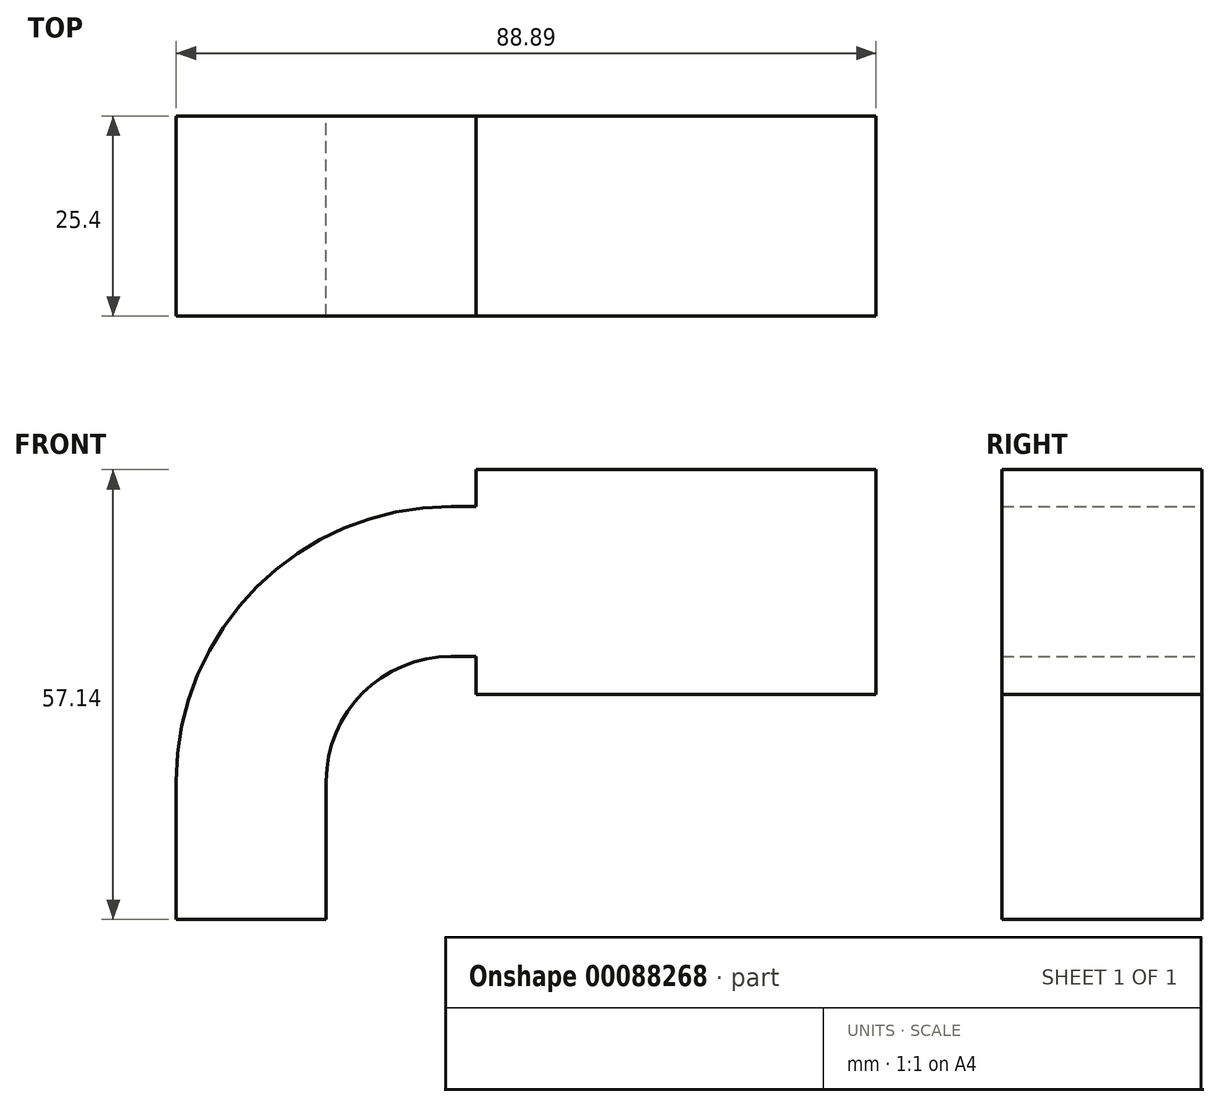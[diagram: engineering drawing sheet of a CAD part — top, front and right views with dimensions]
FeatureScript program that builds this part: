
annotation { "Feature Type Name" : "Feature", "Feature Type Description" : "" }
export const myFeature = defineFeature(function(context is Context, id is Id, definition is map)
    precondition{}
    {
        {
            var Q0;
            Q0=qCreatedBy(makeId("Front.planeOp"),FACE);
            var sketch = newSketch(context, id + "F0", { "sketchPlane" : qUnion([Q0])});
            skLineSegment(sketch, "E0.bottom", {"start": v(41.27, 9.53) * mm, "end": v(-41.28, 9.53) * mm});
            skLineSegment(sketch, "E0.top", {"start": v(41.28, -9.52) * mm, "end": v(-41.28, -9.53) * mm});
            skLineSegment(sketch, "E0.left", {"start": v(41.28, 9.53) * mm, "end": v(41.28, -9.52) * mm});
            skLineSegment(sketch, "E0.right", {"start": v(-41.28, 9.53) * mm, "end": v(-41.28, -9.53) * mm});
            skPoint(sketch, "E0.middle", {"position": v(0, 0) * mm});
            skLineSegment(sketch, "E1.bottom", {"start": v(111.12, 38.1) * mm, "end": v(60.32, 38.1) * mm});
            skLineSegment(sketch, "E1.right", {"start": v(60.32, 38.1) * mm, "end": v(60.32, 61.98) * mm});
            skPoint(sketch, "E1.middle", {"position": v(85.72, 52.39) * mm});
            skLineSegment(sketch, "E2", {"start": v(41.27, 9.53) * mm, "end": v(41.27, 27.05) * mm});
            skArc(sketch, "E3", {"start": v(41.27, 42.89) * mm, "mid": v(41.29, 42.92) * mm, "end": v(41.31, 42.93) * mm});
            skLineSegment(sketch, "E4", {"start": v(57.15, 42.93) * mm, "end": v(85.72, 42.93) * mm});
            skArc(sketch, "E5.filletArc", {"start": v(57.15, 42.93) * mm, "mid": v(45.92, 38.28) * mm, "end": v(41.27, 27.05) * mm});
            skLineSegment(sketch, "E6.0", {"start": v(57.15, 61.98) * mm, "end": v(85.72, 61.98) * mm});
            skArc(sketch, "E6.1", {"start": v(57.15, 61.98) * mm, "mid": v(32.45, 51.75) * mm, "end": v(22.22, 27.05) * mm});
            skLineSegment(sketch, "E6.2", {"start": v(22.22, 9.53) * mm, "end": v(22.22, 27.05) * mm});
            skPoint(sketch, "E7.start.orphan", {"position": v(92.08, 66.68) * mm});
            skPoint(sketch, "E8.orphan", {"position": v(60.32, 66.68) * mm});
            skPoint(sketch, "E1.left.end.orphan", {"position": v(111.12, 66.68) * mm});
            skLineSegment(sketch, "E9", {"start": v(111.12, 66.68) * mm, "end": v(111.12, 38.1) * mm});
            skLineSegment(sketch, "E10", {"start": v(60.32, 61.98) * mm, "end": v(60.32, 66.68) * mm});
            skLineSegment(sketch, "E11", {"start": v(60.32, 66.68) * mm, "end": v(111.12, 66.68) * mm});
            skFitSpline(sketch, "E12", {"points": [v(-41.28, 9.52) * mm, v(57.15, 61.98) * mm], "startDerivative": vector(15.7, 135.95) * mm, "endDerivative": vector(115.79, 7.45) * mm});
            skLineSegment(sketch, "E13", {"start": v(85.72, 66.68) * mm, "end": v(85.72, 38.1) * mm});
            skPoint(sketch, "E14.orphan", {"position": v(92.08, 61.98) * mm});
            skSolve(sketch);
        }
        {
            var Q0;
            {var subQ0=sQuery(id+"F0.wireOp",EDGE,"E12");var subQ1=sQuery(id+"F0.wireOp",EDGE,"E6.1");var subQ3=makeQuery(id+"F0.imprint","INTERSECT",VERTEX,{"derivedFrom":[subQ1,subQ0]});Q0=makeQuery(id+"F0.imprint","IMPRINT",FACE,{"disambiguationData":[TD([[makeQuery(id+"F0.imprint","IMPRINT",EDGE,{"disambiguationData":[TD([[subQ3,1.0]])],"derivedFrom":subQ1}),1.0]])]});}
            var Q1;
            {var subQ0=sQuery(id+"F0.wireOp",EDGE,"E1.right");var subQ1=sQuery(id+"F0.wireOp",EDGE,"E1.bottom");var subQ2=makeQuery(id+"F0.imprint","INTERSECT",VERTEX,{"derivedFrom":[subQ1,subQ0]});Q1=makeQuery(id+"F0.imprint","IMPRINT",FACE,{"disambiguationData":[TD([[makeQuery(id+"F0.imprint","IMPRINT",EDGE,{"disambiguationData":[TD([[subQ2,1.0]])],"derivedFrom":subQ1}),-1.0]])]});}
            var Q2;
            {var subQ0=sQuery(id+"F0.wireOp",EDGE,"E10");Q2=makeQuery(id+"F0.imprint","IMPRINT",FACE,{"disambiguationData":[TD([[makeQuery(id+"F0.imprint","IMPRINT",EDGE,{"derivedFrom":subQ0}),-1.0]])]});}
            var Q3;
            {var subQ4=sQuery(id+"F0.wireOp",EDGE,"E9");Q3=makeQuery(id+"F0.imprint","IMPRINT",FACE,{"disambiguationData":[TD([[makeQuery(id+"F0.imprint","IMPRINT",EDGE,{"derivedFrom":subQ4}),-1.0]])]});}
            var Q4;
            {var subQ4=sQuery(id+"F0.wireOp",EDGE,"E2");Q4=makeQuery(id+"F0.imprint","IMPRINT",FACE,{"disambiguationData":[TD([[makeQuery(id+"F0.imprint","IMPRINT",EDGE,{"derivedFrom":subQ4}),1.0]])]});}
            var Q5;
            {var subQ3=sQuery(id+"F0.wireOp",EDGE,"E4");var subQ5=sQuery(id+"F0.wireOp",EDGE,"E13");var subQ6=makeQuery(id+"F0.imprint","INTERSECT",VERTEX,{"derivedFrom":[subQ3,subQ5]});Q5=makeQuery(id+"F0.imprint","IMPRINT",FACE,{"disambiguationData":[TD([[makeQuery(id+"F0.imprint","IMPRINT",EDGE,{"disambiguationData":[TD([[subQ6,1.0]])],"derivedFrom":subQ3}),1.0]])]});}
            extrude(context, id + "F1", {"entities" : qUnion([Q0, Q1, Q2, Q3, Q4, Q5]), "endBound" : BoundingType.SYMMETRIC, "depth" : 25.4 * mm});
        }
    });
